SOLIDWORKS PART (.sldprt)
format: sldprt  version: not decoded by parser v0  size: 116,224 bytes
history: native  units: mm
features: sketch x5, plane x4, extrude x3, fillet x2, cut_extrude x2, material x1 (+13 scaffold rows collapsed)
feature tree (30):
  scaffold x13  (default folders/planes/origin — collapsed)
  material  "材质 <未指定>"
  plane  "前视基准面"
  plane  "上视基准面"
  plane  "右视基准面"
  sketch  "草图1"  dims[D1=0.5mm]
  extrude  "凸台-拉伸1"  Depth=1mm
  fillet  "圆角1"  Radius=0.1mm
  plane  "基准面1"  Offset=0.3mm
  sketch  "草图2"
  extrude  "凸台-拉伸2"  Depth=40mm
  sketch  "草图3"
  cut_extrude  "切除-拉伸1"  Depth=20mm
  sketch  "草图4"  dims[c1.D1=0.3mm c1.D2=0.5mm c1.D3=~0.583095mm c2.D1=0.3mm]
  extrude  "凸台-拉伸3"  Depth=5.5mm
  sketch  "草图6"  dims[D1=0.3mm]
  cut_extrude  "切除-拉伸2"  Depth=5.5mm
  fillet  "圆角2"  Radius=0.3mm
decode coverage: 10 of 12 modeling features carry decoded parameters
note: ~ marks probable driven/reference dimensions
note: suppression state not decoded; provenance and decode notes live in map.json
